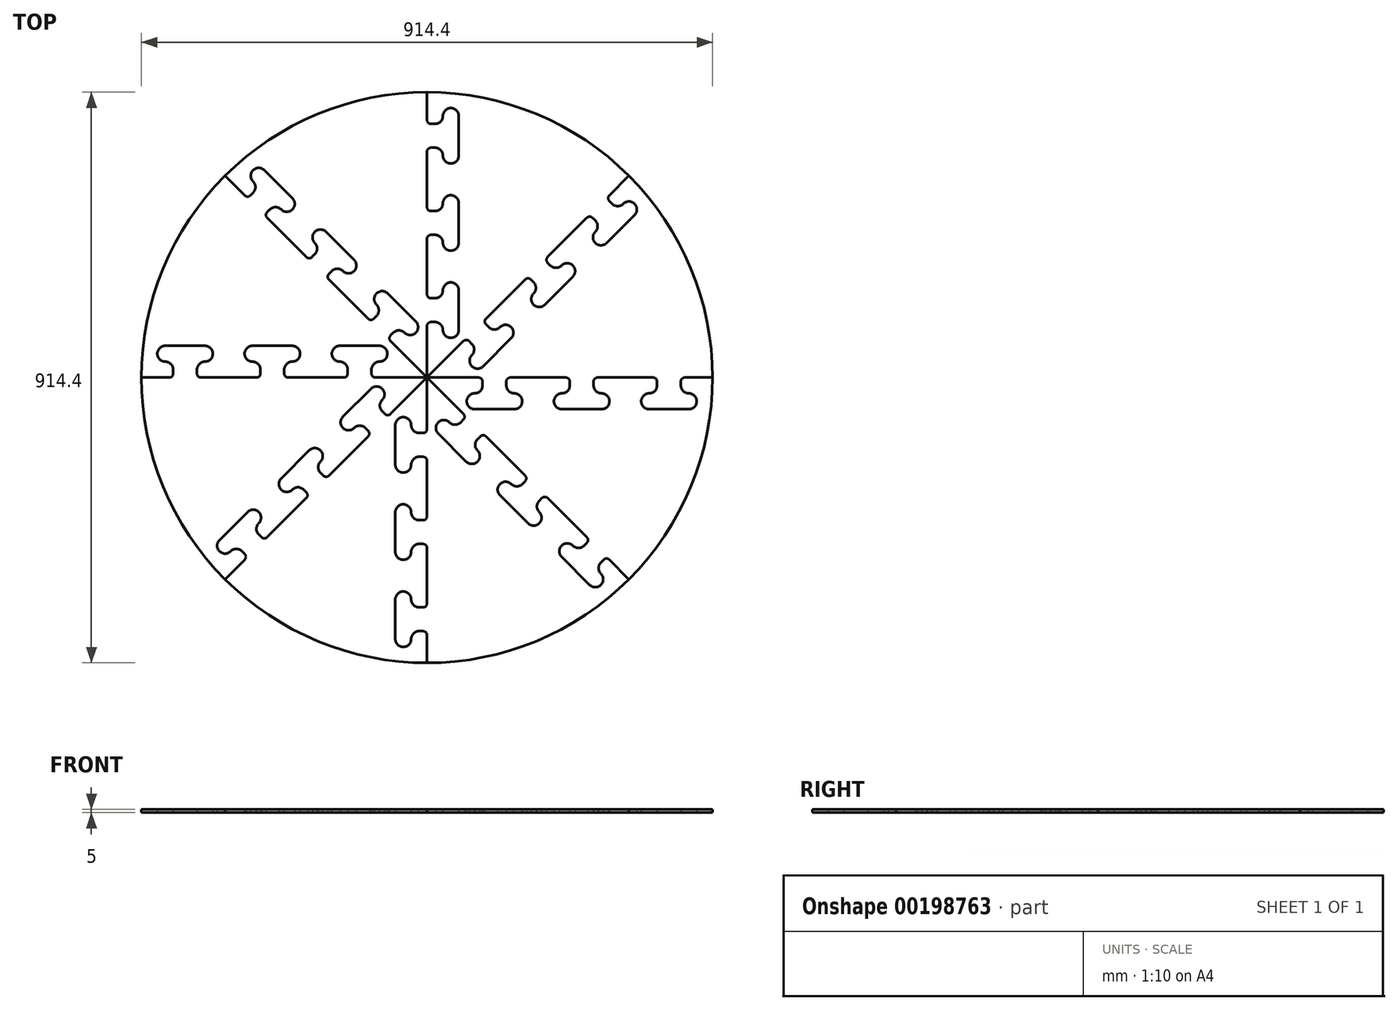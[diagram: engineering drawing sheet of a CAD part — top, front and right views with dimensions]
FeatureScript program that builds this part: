
annotation { "Feature Type Name" : "Feature", "Feature Type Description" : "" }
export const myFeature = defineFeature(function(context is Context, id is Id, definition is map)
    precondition{}
    {
        {
            var Q0;
            Q0=qCreatedBy(makeId("Top.planeOp"),FACE);
            var sketch = newSketch(context, id + "F0", { "sketchPlane" : qUnion([Q0])});
            skLineSegment(sketch, "E0", {"start": v(-457.2, 0) * mm, "end": v(-412.75, 0) * mm});
            skLineSegment(sketch, "E1", {"start": v(-406.4, 6.35) * mm, "end": v(-406.4, 12.7) * mm});
            skArc(sketch, "E2", {"start": v(-419.1, 50.8) * mm, "mid": v(-431.8, 38.1) * mm, "end": v(-419.1, 25.4) * mm});
            skLineSegment(sketch, "E3", {"start": v(-387.35, 0) * mm, "end": v(-387.35, 50.8) * mm, "construction": true});
            skLineSegment(sketch, "E4", {"start": v(-419.1, 50.8) * mm, "end": v(-387.35, 50.8) * mm});
            skPoint(sketch, "E5.visualSharp", {"position": v(-406.4, 38.1) * mm});
            skArc(sketch, "E5.filletArc", {"start": v(-406.4, 12.7) * mm, "mid": v(-410.12, 21.68) * mm, "end": v(-419.1, 25.4) * mm});
            skLineSegment(sketch, "E6", {"start": v(-406.4, 0) * mm, "end": v(-387.35, 0) * mm, "construction": true});
            skPoint(sketch, "E7.visualSharp", {"position": v(-406.4, 0) * mm});
            skArc(sketch, "E7.filletArc", {"start": v(-412.75, 0) * mm, "mid": v(-408.26, 1.86) * mm, "end": v(-406.4, 6.35) * mm});
            skLineSegment(sketch, "E8", {"start": v(-406.4, 0) * mm, "end": v(-406.4, 6.35) * mm, "construction": true});
            skLineSegment(sketch, "E9", {"start": v(-412.75, 0) * mm, "end": v(-406.4, 0) * mm, "construction": true});
            skLineSegment(sketch, "E10.MirrorCS", {"start": v(-355.6, 50.8) * mm, "end": v(-387.35, 50.8) * mm});
            skArc(sketch, "E11.MirrorCS", {"start": v(-355.6, 50.8) * mm, "mid": v(-342.9, 38.1) * mm, "end": v(-355.6, 25.4) * mm});
            skArc(sketch, "E12.MirrorCS", {"start": v(-368.3, 12.7) * mm, "mid": v(-364.58, 21.68) * mm, "end": v(-355.6, 25.4) * mm});
            skLineSegment(sketch, "E13.MirrorCS", {"start": v(-368.3, 6.35) * mm, "end": v(-368.3, 12.7) * mm});
            skArc(sketch, "E14.MirrorCS", {"start": v(-361.95, 0) * mm, "mid": v(-366.44, 1.86) * mm, "end": v(-368.3, 6.35) * mm});
            skLineSegment(sketch, "E15.1.0.0", {"start": v(-247.65, 0) * mm, "end": v(-247.65, 50.8) * mm, "construction": true});
            skPoint(sketch, "E15.1.0.1", {"position": v(-266.7, 38.1) * mm});
            skPoint(sketch, "E15.1.0.2", {"position": v(-266.7, 0) * mm});
            skArc(sketch, "E15.1.0.3", {"start": v(-279.4, 50.8) * mm, "mid": v(-292.1, 38.1) * mm, "end": v(-279.4, 25.4) * mm});
            skLineSegment(sketch, "E15.1.0.5", {"start": v(-266.7, 0) * mm, "end": v(-247.65, 0) * mm, "construction": true});
            skLineSegment(sketch, "E15.1.0.6", {"start": v(-215.9, 50.8) * mm, "end": v(-247.65, 50.8) * mm});
            skLineSegment(sketch, "E15.1.0.7", {"start": v(-279.4, 50.8) * mm, "end": v(-247.65, 50.8) * mm});
            skArc(sketch, "E15.1.0.8", {"start": v(-215.9, 50.8) * mm, "mid": v(-203.2, 38.1) * mm, "end": v(-215.9, 25.4) * mm});
            skLineSegment(sketch, "E15.1.0.9", {"start": v(-317.5, 0) * mm, "end": v(-273.05, 0) * mm});
            skArc(sketch, "E15.1.0.10", {"start": v(-266.7, 12.7) * mm, "mid": v(-270.42, 21.68) * mm, "end": v(-279.4, 25.4) * mm});
            skArc(sketch, "E15.1.0.11", {"start": v(-222.25, 0) * mm, "mid": v(-226.74, 1.86) * mm, "end": v(-228.6, 6.35) * mm});
            skArc(sketch, "E15.1.0.12", {"start": v(-228.6, 12.7) * mm, "mid": v(-224.88, 21.68) * mm, "end": v(-215.9, 25.4) * mm});
            skLineSegment(sketch, "E15.1.0.13", {"start": v(-228.6, 6.35) * mm, "end": v(-228.6, 12.7) * mm});
            skLineSegment(sketch, "E15.1.0.14", {"start": v(-266.7, 6.35) * mm, "end": v(-266.7, 12.7) * mm});
            skArc(sketch, "E15.1.0.15", {"start": v(-273.05, 0) * mm, "mid": v(-268.56, 1.86) * mm, "end": v(-266.7, 6.35) * mm});
            skLineSegment(sketch, "E15.1.0.16", {"start": v(-266.7, 0) * mm, "end": v(-266.7, 6.35) * mm, "construction": true});
            skLineSegment(sketch, "E15.1.0.17", {"start": v(-273.05, 0) * mm, "end": v(-266.7, 0) * mm, "construction": true});
            skLineSegment(sketch, "E15.2.0.0", {"start": v(-107.95, 0) * mm, "end": v(-107.95, 50.8) * mm, "construction": true});
            skPoint(sketch, "E15.2.0.1", {"position": v(-127, 38.1) * mm});
            skArc(sketch, "E15.2.0.3", {"start": v(-139.7, 50.8) * mm, "mid": v(-152.4, 38.1) * mm, "end": v(-139.7, 25.4) * mm});
            skLineSegment(sketch, "E15.2.0.5", {"start": v(-127, 0) * mm, "end": v(-107.95, 0) * mm, "construction": true});
            skLineSegment(sketch, "E15.2.0.6", {"start": v(-76.2, 50.8) * mm, "end": v(-107.95, 50.8) * mm});
            skLineSegment(sketch, "E15.2.0.7", {"start": v(-139.7, 50.8) * mm, "end": v(-107.95, 50.8) * mm});
            skArc(sketch, "E15.2.0.8", {"start": v(-76.2, 50.8) * mm, "mid": v(-63.5, 38.1) * mm, "end": v(-76.2, 25.4) * mm});
            skLineSegment(sketch, "E15.2.0.9", {"start": v(-177.8, 0) * mm, "end": v(-133.35, 0) * mm});
            skArc(sketch, "E15.2.0.10", {"start": v(-127, 12.7) * mm, "mid": v(-130.72, 21.68) * mm, "end": v(-139.7, 25.4) * mm});
            skArc(sketch, "E15.2.0.11", {"start": v(-82.55, 0) * mm, "mid": v(-87.04, 1.86) * mm, "end": v(-88.9, 6.35) * mm});
            skArc(sketch, "E15.2.0.12", {"start": v(-88.9, 12.7) * mm, "mid": v(-85.18, 21.68) * mm, "end": v(-76.2, 25.4) * mm});
            skLineSegment(sketch, "E15.2.0.13", {"start": v(-88.9, 6.35) * mm, "end": v(-88.9, 12.7) * mm});
            skLineSegment(sketch, "E15.2.0.14", {"start": v(-127, 6.35) * mm, "end": v(-127, 12.7) * mm});
            skArc(sketch, "E15.2.0.15", {"start": v(-133.35, 0) * mm, "mid": v(-128.86, 1.86) * mm, "end": v(-127, 6.35) * mm});
            skLineSegment(sketch, "E15.2.0.16", {"start": v(-127, 0) * mm, "end": v(-127, 6.35) * mm, "construction": true});
            skLineSegment(sketch, "E15.2.0.17", {"start": v(-133.35, 0) * mm, "end": v(-127, 0) * mm, "construction": true});
            skLineSegment(sketch, "E15.direction1", {"start": v(-457.2, 0) * mm, "end": v(-317.5, 0) * mm, "construction": true});
            skLineSegment(sketch, "E16", {"start": v(-361.95, 0) * mm, "end": v(-317.5, 0) * mm});
            skLineSegment(sketch, "E17", {"start": v(-222.25, 0) * mm, "end": v(-177.8, 0) * mm});
            skLineSegment(sketch, "E18", {"start": v(-82.55, 0) * mm, "end": v(0, 0) * mm});
            skCircle(sketch, "E19.1.0", {"center": v(0, 0) * mm, "radius": 457.2 * mm});
            skLineSegment(sketch, "E20", {"start": v(-419.1, 25.4) * mm, "end": v(-355.6, 25.4) * mm, "construction": true});
            skLineSegment(sketch, "E21.1.0", {"start": v(-224.5, -224.5) * mm, "end": v(-193.08, -193.08) * mm});
            skLineSegment(sketch, "E21.1.1", {"start": v(-89.8, -89.8) * mm, "end": v(-76.33, -76.33) * mm, "construction": true});
            skArc(sketch, "E21.1.2", {"start": v(-296.35, -278.39) * mm, "mid": v(-305.33, -274.67) * mm, "end": v(-314.3, -278.39) * mm});
            skLineSegment(sketch, "E21.1.3", {"start": v(-323.29, -323.29) * mm, "end": v(-224.5, -224.5) * mm, "construction": true});
            skLineSegment(sketch, "E21.1.4", {"start": v(-175.11, -175.11) * mm, "end": v(-211.04, -139.2) * mm, "construction": true});
            skPoint(sketch, "E21.1.5", {"position": v(-188.59, -188.59) * mm});
            skArc(sketch, "E21.1.6", {"start": v(-269.4, -251.45) * mm, "mid": v(-273.13, -242.47) * mm, "end": v(-269.4, -233.49) * mm});
            skLineSegment(sketch, "E21.1.7", {"start": v(-287.37, -215.53) * mm, "end": v(-309.82, -237.98) * mm});
            skLineSegment(sketch, "E21.1.8", {"start": v(-332.27, -260.43) * mm, "end": v(-309.82, -237.98) * mm});
            skPoint(sketch, "E21.1.9", {"position": v(-314.3, -260.43) * mm});
            skArc(sketch, "E21.1.10", {"start": v(-332.27, -260.43) * mm, "mid": v(-332.27, -278.39) * mm, "end": v(-314.3, -278.39) * mm});
            skLineSegment(sketch, "E21.1.11", {"start": v(-273.9, -273.9) * mm, "end": v(-309.82, -237.98) * mm, "construction": true});
            skLineSegment(sketch, "E21.1.12", {"start": v(-157.15, -157.15) * mm, "end": v(-125.72, -125.72) * mm});
            skArc(sketch, "E21.1.13", {"start": v(-197.57, -179.6) * mm, "mid": v(-206.55, -175.89) * mm, "end": v(-215.53, -179.6) * mm});
            skArc(sketch, "E21.1.14", {"start": v(-89.8, -17.96) * mm, "mid": v(-71.84, -17.96) * mm, "end": v(-71.84, -35.92) * mm});
            skArc(sketch, "E21.1.15", {"start": v(-233.49, -161.64) * mm, "mid": v(-233.49, -179.6) * mm, "end": v(-215.53, -179.6) * mm});
            skLineSegment(sketch, "E21.1.16", {"start": v(-188.59, -188.59) * mm, "end": v(-175.11, -175.11) * mm, "construction": true});
            skArc(sketch, "E21.1.17", {"start": v(-98.78, -80.82) * mm, "mid": v(-107.76, -77.1) * mm, "end": v(-116.74, -80.82) * mm});
            skLineSegment(sketch, "E21.1.18", {"start": v(-233.49, -161.64) * mm, "end": v(-211.04, -139.2) * mm});
            skLineSegment(sketch, "E21.1.19", {"start": v(-134.7, -62.86) * mm, "end": v(-112.25, -40.41) * mm});
            skLineSegment(sketch, "E21.1.20", {"start": v(-188.59, -116.74) * mm, "end": v(-211.04, -139.2) * mm});
            skLineSegment(sketch, "E21.1.21", {"start": v(-314.3, -278.39) * mm, "end": v(-269.4, -233.49) * mm, "construction": true});
            skLineSegment(sketch, "E21.1.22", {"start": v(-76.33, -76.33) * mm, "end": v(-112.25, -40.41) * mm, "construction": true});
            skPoint(sketch, "E21.1.23", {"position": v(-116.74, -62.86) * mm});
            skLineSegment(sketch, "E21.1.24", {"start": v(-125.72, -125.72) * mm, "end": v(-94.3, -94.3) * mm});
            skLineSegment(sketch, "E21.1.25", {"start": v(-58.37, -58.37) * mm, "end": v(0, 0) * mm});
            skLineSegment(sketch, "E21.1.26", {"start": v(-89.8, -17.96) * mm, "end": v(-112.25, -40.41) * mm});
            skArc(sketch, "E21.1.27", {"start": v(-188.59, -116.74) * mm, "mid": v(-170.62, -116.74) * mm, "end": v(-170.62, -134.7) * mm});
            skArc(sketch, "E21.1.28", {"start": v(-71.84, -53.88) * mm, "mid": v(-75.56, -44.9) * mm, "end": v(-71.84, -35.92) * mm});
            skPoint(sketch, "E21.1.29", {"position": v(-287.37, -287.37) * mm});
            skArc(sketch, "E21.1.30", {"start": v(-170.62, -152.66) * mm, "mid": v(-174.34, -143.68) * mm, "end": v(-170.62, -134.7) * mm});
            skArc(sketch, "E21.1.31", {"start": v(-134.7, -62.86) * mm, "mid": v(-134.7, -80.82) * mm, "end": v(-116.74, -80.82) * mm});
            skPoint(sketch, "E21.1.32", {"position": v(-215.53, -161.64) * mm});
            skArc(sketch, "E21.1.33", {"start": v(-287.37, -215.53) * mm, "mid": v(-269.4, -215.53) * mm, "end": v(-269.4, -233.49) * mm});
            skLineSegment(sketch, "E21.1.34", {"start": v(-255.94, -255.94) * mm, "end": v(-224.5, -224.5) * mm});
            skLineSegment(sketch, "E21.1.35", {"start": v(-323.29, -323.29) * mm, "end": v(-291.86, -291.86) * mm});
            skLineSegment(sketch, "E21.1.36", {"start": v(-287.37, -287.37) * mm, "end": v(-273.9, -273.9) * mm, "construction": true});
            skLineSegment(sketch, "E21.1.37", {"start": v(-193.08, -184.1) * mm, "end": v(-197.57, -179.6) * mm});
            skLineSegment(sketch, "E21.1.38", {"start": v(-264.92, -255.94) * mm, "end": v(-269.4, -251.45) * mm});
            skLineSegment(sketch, "E21.1.39", {"start": v(-166.13, -157.15) * mm, "end": v(-170.62, -152.66) * mm});
            skArc(sketch, "E21.1.40", {"start": v(-255.94, -255.94) * mm, "mid": v(-260.43, -257.8) * mm, "end": v(-264.92, -255.94) * mm});
            skLineSegment(sketch, "E21.1.41", {"start": v(-94.3, -85.31) * mm, "end": v(-98.78, -80.82) * mm});
            skArc(sketch, "E21.1.42", {"start": v(-157.15, -157.15) * mm, "mid": v(-161.64, -159.01) * mm, "end": v(-166.13, -157.15) * mm});
            skLineSegment(sketch, "E21.1.43", {"start": v(-291.86, -282.88) * mm, "end": v(-296.35, -278.39) * mm});
            skArc(sketch, "E21.1.44", {"start": v(-58.37, -58.37) * mm, "mid": v(-62.86, -60.23) * mm, "end": v(-67.35, -58.37) * mm});
            skLineSegment(sketch, "E21.1.45", {"start": v(-67.35, -58.37) * mm, "end": v(-71.84, -53.88) * mm});
            skArc(sketch, "E21.1.46", {"start": v(-94.3, -94.3) * mm, "mid": v(-92.43, -89.8) * mm, "end": v(-94.3, -85.31) * mm});
            skLineSegment(sketch, "E21.1.47", {"start": v(-291.86, -291.86) * mm, "end": v(-287.37, -287.37) * mm, "construction": true});
            skLineSegment(sketch, "E21.1.48", {"start": v(-94.3, -94.3) * mm, "end": v(-89.8, -89.8) * mm, "construction": true});
            skLineSegment(sketch, "E21.1.49", {"start": v(-193.08, -193.08) * mm, "end": v(-188.59, -188.59) * mm, "construction": true});
            skLineSegment(sketch, "E21.1.50", {"start": v(-188.59, -188.59) * mm, "end": v(-193.08, -184.1) * mm, "construction": true});
            skLineSegment(sketch, "E21.1.51", {"start": v(-89.8, -89.8) * mm, "end": v(-94.3, -85.31) * mm, "construction": true});
            skLineSegment(sketch, "E21.1.52", {"start": v(-287.37, -287.37) * mm, "end": v(-291.86, -282.88) * mm, "construction": true});
            skArc(sketch, "E21.1.53", {"start": v(-193.08, -193.08) * mm, "mid": v(-191.22, -188.59) * mm, "end": v(-193.08, -184.1) * mm});
            skArc(sketch, "E21.1.54", {"start": v(-291.86, -291.86) * mm, "mid": v(-290, -287.37) * mm, "end": v(-291.86, -282.88) * mm});
            skLineSegment(sketch, "E21.2.0", {"start": v(0, -317.5) * mm, "end": v(0, -273.05) * mm});
            skLineSegment(sketch, "E21.2.1", {"start": v(0, -127) * mm, "end": v(0, -107.95) * mm, "construction": true});
            skArc(sketch, "E21.2.2", {"start": v(-12.7, -406.4) * mm, "mid": v(-21.68, -410.12) * mm, "end": v(-25.4, -419.1) * mm});
            skLineSegment(sketch, "E21.2.3", {"start": v(0, -457.2) * mm, "end": v(0, -317.5) * mm, "construction": true});
            skLineSegment(sketch, "E21.2.4", {"start": v(0, -247.65) * mm, "end": v(-50.8, -247.65) * mm, "construction": true});
            skPoint(sketch, "E21.2.5", {"position": v(0, -266.7) * mm});
            skArc(sketch, "E21.2.6", {"start": v(-12.7, -368.3) * mm, "mid": v(-21.68, -364.58) * mm, "end": v(-25.4, -355.6) * mm});
            skLineSegment(sketch, "E21.2.7", {"start": v(-50.8, -355.6) * mm, "end": v(-50.8, -387.35) * mm});
            skLineSegment(sketch, "E21.2.8", {"start": v(-50.8, -419.1) * mm, "end": v(-50.8, -387.35) * mm});
            skPoint(sketch, "E21.2.9", {"position": v(-38.1, -406.4) * mm});
            skArc(sketch, "E21.2.10", {"start": v(-50.8, -419.1) * mm, "mid": v(-38.1, -431.8) * mm, "end": v(-25.4, -419.1) * mm});
            skLineSegment(sketch, "E21.2.11", {"start": v(0, -387.35) * mm, "end": v(-50.8, -387.35) * mm, "construction": true});
            skLineSegment(sketch, "E21.2.12", {"start": v(0, -222.25) * mm, "end": v(0, -177.8) * mm});
            skArc(sketch, "E21.2.13", {"start": v(-12.7, -266.7) * mm, "mid": v(-21.68, -270.42) * mm, "end": v(-25.4, -279.4) * mm});
            skArc(sketch, "E21.2.14", {"start": v(-50.8, -76.2) * mm, "mid": v(-38.1, -63.5) * mm, "end": v(-25.4, -76.2) * mm});
            skArc(sketch, "E21.2.15", {"start": v(-50.8, -279.4) * mm, "mid": v(-38.1, -292.1) * mm, "end": v(-25.4, -279.4) * mm});
            skLineSegment(sketch, "E21.2.16", {"start": v(0, -266.7) * mm, "end": v(0, -247.65) * mm, "construction": true});
            skArc(sketch, "E21.2.17", {"start": v(-12.7, -127) * mm, "mid": v(-21.68, -130.72) * mm, "end": v(-25.4, -139.7) * mm});
            skLineSegment(sketch, "E21.2.18", {"start": v(-50.8, -279.4) * mm, "end": v(-50.8, -247.65) * mm});
            skLineSegment(sketch, "E21.2.19", {"start": v(-50.8, -139.7) * mm, "end": v(-50.8, -107.95) * mm});
            skLineSegment(sketch, "E21.2.20", {"start": v(-50.8, -215.9) * mm, "end": v(-50.8, -247.65) * mm});
            skLineSegment(sketch, "E21.2.21", {"start": v(-25.4, -419.1) * mm, "end": v(-25.4, -355.6) * mm, "construction": true});
            skLineSegment(sketch, "E21.2.22", {"start": v(0, -107.95) * mm, "end": v(-50.8, -107.95) * mm, "construction": true});
            skPoint(sketch, "E21.2.23", {"position": v(-38.1, -127) * mm});
            skLineSegment(sketch, "E21.2.24", {"start": v(0, -177.8) * mm, "end": v(0, -133.35) * mm});
            skLineSegment(sketch, "E21.2.25", {"start": v(0, -82.55) * mm, "end": v(0, 0) * mm});
            skLineSegment(sketch, "E21.2.26", {"start": v(-50.8, -76.2) * mm, "end": v(-50.8, -107.95) * mm});
            skArc(sketch, "E21.2.27", {"start": v(-50.8, -215.9) * mm, "mid": v(-38.1, -203.2) * mm, "end": v(-25.4, -215.9) * mm});
            skArc(sketch, "E21.2.28", {"start": v(-12.7, -88.9) * mm, "mid": v(-21.68, -85.18) * mm, "end": v(-25.4, -76.2) * mm});
            skPoint(sketch, "E21.2.29", {"position": v(0, -406.4) * mm});
            skArc(sketch, "E21.2.30", {"start": v(-12.7, -228.6) * mm, "mid": v(-21.68, -224.88) * mm, "end": v(-25.4, -215.9) * mm});
            skArc(sketch, "E21.2.31", {"start": v(-50.8, -139.7) * mm, "mid": v(-38.1, -152.4) * mm, "end": v(-25.4, -139.7) * mm});
            skPoint(sketch, "E21.2.32", {"position": v(-38.1, -266.7) * mm});
            skArc(sketch, "E21.2.33", {"start": v(-50.8, -355.6) * mm, "mid": v(-38.1, -342.9) * mm, "end": v(-25.4, -355.6) * mm});
            skLineSegment(sketch, "E21.2.34", {"start": v(0, -361.95) * mm, "end": v(0, -317.5) * mm});
            skLineSegment(sketch, "E21.2.35", {"start": v(0, -457.2) * mm, "end": v(0, -412.75) * mm});
            skLineSegment(sketch, "E21.2.36", {"start": v(0, -406.4) * mm, "end": v(0, -387.35) * mm, "construction": true});
            skLineSegment(sketch, "E21.2.37", {"start": v(-6.35, -266.7) * mm, "end": v(-12.7, -266.7) * mm});
            skLineSegment(sketch, "E21.2.38", {"start": v(-6.35, -368.3) * mm, "end": v(-12.7, -368.3) * mm});
            skLineSegment(sketch, "E21.2.39", {"start": v(-6.35, -228.6) * mm, "end": v(-12.7, -228.6) * mm});
            skArc(sketch, "E21.2.40", {"start": v(0, -361.95) * mm, "mid": v(-1.86, -366.44) * mm, "end": v(-6.35, -368.3) * mm});
            skLineSegment(sketch, "E21.2.41", {"start": v(-6.35, -127) * mm, "end": v(-12.7, -127) * mm});
            skArc(sketch, "E21.2.42", {"start": v(0, -222.25) * mm, "mid": v(-1.86, -226.74) * mm, "end": v(-6.35, -228.6) * mm});
            skLineSegment(sketch, "E21.2.43", {"start": v(-6.35, -406.4) * mm, "end": v(-12.7, -406.4) * mm});
            skArc(sketch, "E21.2.44", {"start": v(0, -82.55) * mm, "mid": v(-1.86, -87.04) * mm, "end": v(-6.35, -88.9) * mm});
            skLineSegment(sketch, "E21.2.45", {"start": v(-6.35, -88.9) * mm, "end": v(-12.7, -88.9) * mm});
            skArc(sketch, "E21.2.46", {"start": v(0, -133.35) * mm, "mid": v(-1.86, -128.86) * mm, "end": v(-6.35, -127) * mm});
            skLineSegment(sketch, "E21.2.47", {"start": v(0, -412.75) * mm, "end": v(0, -406.4) * mm, "construction": true});
            skLineSegment(sketch, "E21.2.48", {"start": v(0, -133.35) * mm, "end": v(0, -127) * mm, "construction": true});
            skLineSegment(sketch, "E21.2.49", {"start": v(0, -273.05) * mm, "end": v(0, -266.7) * mm, "construction": true});
            skLineSegment(sketch, "E21.2.50", {"start": v(0, -266.7) * mm, "end": v(-6.35, -266.7) * mm, "construction": true});
            skLineSegment(sketch, "E21.2.51", {"start": v(0, -127) * mm, "end": v(-6.35, -127) * mm, "construction": true});
            skLineSegment(sketch, "E21.2.52", {"start": v(0, -406.4) * mm, "end": v(-6.35, -406.4) * mm, "construction": true});
            skArc(sketch, "E21.2.53", {"start": v(0, -273.05) * mm, "mid": v(-1.86, -268.56) * mm, "end": v(-6.35, -266.7) * mm});
            skArc(sketch, "E21.2.54", {"start": v(0, -412.75) * mm, "mid": v(-1.86, -408.26) * mm, "end": v(-6.35, -406.4) * mm});
            skLineSegment(sketch, "E21.3.0", {"start": v(224.5, -224.5) * mm, "end": v(193.08, -193.08) * mm});
            skLineSegment(sketch, "E21.3.1", {"start": v(89.8, -89.8) * mm, "end": v(76.33, -76.33) * mm, "construction": true});
            skArc(sketch, "E21.3.2", {"start": v(278.39, -296.35) * mm, "mid": v(274.67, -305.33) * mm, "end": v(278.39, -314.3) * mm});
            skLineSegment(sketch, "E21.3.3", {"start": v(323.29, -323.29) * mm, "end": v(224.5, -224.5) * mm, "construction": true});
            skLineSegment(sketch, "E21.3.4", {"start": v(175.11, -175.11) * mm, "end": v(139.2, -211.04) * mm, "construction": true});
            skPoint(sketch, "E21.3.5", {"position": v(188.59, -188.59) * mm});
            skArc(sketch, "E21.3.6", {"start": v(251.45, -269.4) * mm, "mid": v(242.47, -273.13) * mm, "end": v(233.49, -269.4) * mm});
            skLineSegment(sketch, "E21.3.7", {"start": v(215.53, -287.37) * mm, "end": v(237.98, -309.82) * mm});
            skLineSegment(sketch, "E21.3.8", {"start": v(260.43, -332.27) * mm, "end": v(237.98, -309.82) * mm});
            skPoint(sketch, "E21.3.9", {"position": v(260.43, -314.3) * mm});
            skArc(sketch, "E21.3.10", {"start": v(260.43, -332.27) * mm, "mid": v(278.39, -332.27) * mm, "end": v(278.39, -314.3) * mm});
            skLineSegment(sketch, "E21.3.11", {"start": v(273.9, -273.9) * mm, "end": v(237.98, -309.82) * mm, "construction": true});
            skLineSegment(sketch, "E21.3.12", {"start": v(157.15, -157.15) * mm, "end": v(125.72, -125.72) * mm});
            skArc(sketch, "E21.3.13", {"start": v(179.6, -197.57) * mm, "mid": v(175.89, -206.55) * mm, "end": v(179.6, -215.53) * mm});
            skArc(sketch, "E21.3.14", {"start": v(17.96, -89.8) * mm, "mid": v(17.96, -71.84) * mm, "end": v(35.92, -71.84) * mm});
            skArc(sketch, "E21.3.15", {"start": v(161.64, -233.49) * mm, "mid": v(179.6, -233.49) * mm, "end": v(179.6, -215.53) * mm});
            skLineSegment(sketch, "E21.3.16", {"start": v(188.59, -188.59) * mm, "end": v(175.11, -175.11) * mm, "construction": true});
            skArc(sketch, "E21.3.17", {"start": v(80.82, -98.78) * mm, "mid": v(77.1, -107.76) * mm, "end": v(80.82, -116.74) * mm});
            skLineSegment(sketch, "E21.3.18", {"start": v(161.64, -233.49) * mm, "end": v(139.2, -211.04) * mm});
            skLineSegment(sketch, "E21.3.19", {"start": v(62.86, -134.7) * mm, "end": v(40.41, -112.25) * mm});
            skLineSegment(sketch, "E21.3.20", {"start": v(116.74, -188.59) * mm, "end": v(139.2, -211.04) * mm});
            skLineSegment(sketch, "E21.3.21", {"start": v(278.39, -314.3) * mm, "end": v(233.49, -269.4) * mm, "construction": true});
            skLineSegment(sketch, "E21.3.22", {"start": v(76.33, -76.33) * mm, "end": v(40.41, -112.25) * mm, "construction": true});
            skPoint(sketch, "E21.3.23", {"position": v(62.86, -116.74) * mm});
            skLineSegment(sketch, "E21.3.24", {"start": v(125.72, -125.72) * mm, "end": v(94.3, -94.3) * mm});
            skLineSegment(sketch, "E21.3.25", {"start": v(58.37, -58.37) * mm, "end": v(0, 0) * mm});
            skLineSegment(sketch, "E21.3.26", {"start": v(17.96, -89.8) * mm, "end": v(40.41, -112.25) * mm});
            skArc(sketch, "E21.3.27", {"start": v(116.74, -188.59) * mm, "mid": v(116.74, -170.62) * mm, "end": v(134.7, -170.62) * mm});
            skArc(sketch, "E21.3.28", {"start": v(53.88, -71.84) * mm, "mid": v(44.9, -75.56) * mm, "end": v(35.92, -71.84) * mm});
            skPoint(sketch, "E21.3.29", {"position": v(287.37, -287.37) * mm});
            skArc(sketch, "E21.3.30", {"start": v(152.66, -170.62) * mm, "mid": v(143.68, -174.34) * mm, "end": v(134.7, -170.62) * mm});
            skArc(sketch, "E21.3.31", {"start": v(62.86, -134.7) * mm, "mid": v(80.82, -134.7) * mm, "end": v(80.82, -116.74) * mm});
            skPoint(sketch, "E21.3.32", {"position": v(161.64, -215.53) * mm});
            skArc(sketch, "E21.3.33", {"start": v(215.53, -287.37) * mm, "mid": v(215.53, -269.4) * mm, "end": v(233.49, -269.4) * mm});
            skLineSegment(sketch, "E21.3.34", {"start": v(255.94, -255.94) * mm, "end": v(224.5, -224.5) * mm});
            skLineSegment(sketch, "E21.3.35", {"start": v(323.29, -323.29) * mm, "end": v(291.86, -291.86) * mm});
            skLineSegment(sketch, "E21.3.36", {"start": v(287.37, -287.37) * mm, "end": v(273.9, -273.9) * mm, "construction": true});
            skLineSegment(sketch, "E21.3.37", {"start": v(184.1, -193.08) * mm, "end": v(179.6, -197.57) * mm});
            skLineSegment(sketch, "E21.3.38", {"start": v(255.94, -264.92) * mm, "end": v(251.45, -269.4) * mm});
            skLineSegment(sketch, "E21.3.39", {"start": v(157.15, -166.13) * mm, "end": v(152.66, -170.62) * mm});
            skArc(sketch, "E21.3.40", {"start": v(255.94, -255.94) * mm, "mid": v(257.8, -260.43) * mm, "end": v(255.94, -264.92) * mm});
            skLineSegment(sketch, "E21.3.41", {"start": v(85.31, -94.3) * mm, "end": v(80.82, -98.78) * mm});
            skArc(sketch, "E21.3.42", {"start": v(157.15, -157.15) * mm, "mid": v(159.01, -161.64) * mm, "end": v(157.15, -166.13) * mm});
            skLineSegment(sketch, "E21.3.43", {"start": v(282.88, -291.86) * mm, "end": v(278.39, -296.35) * mm});
            skArc(sketch, "E21.3.44", {"start": v(58.37, -58.37) * mm, "mid": v(60.23, -62.86) * mm, "end": v(58.37, -67.35) * mm});
            skLineSegment(sketch, "E21.3.45", {"start": v(58.37, -67.35) * mm, "end": v(53.88, -71.84) * mm});
            skArc(sketch, "E21.3.46", {"start": v(94.3, -94.3) * mm, "mid": v(89.8, -92.43) * mm, "end": v(85.31, -94.3) * mm});
            skLineSegment(sketch, "E21.3.47", {"start": v(291.86, -291.86) * mm, "end": v(287.37, -287.37) * mm, "construction": true});
            skLineSegment(sketch, "E21.3.48", {"start": v(94.3, -94.3) * mm, "end": v(89.8, -89.8) * mm, "construction": true});
            skLineSegment(sketch, "E21.3.49", {"start": v(193.08, -193.08) * mm, "end": v(188.59, -188.59) * mm, "construction": true});
            skLineSegment(sketch, "E21.3.50", {"start": v(188.59, -188.59) * mm, "end": v(184.1, -193.08) * mm, "construction": true});
            skLineSegment(sketch, "E21.3.51", {"start": v(89.8, -89.8) * mm, "end": v(85.31, -94.3) * mm, "construction": true});
            skLineSegment(sketch, "E21.3.52", {"start": v(287.37, -287.37) * mm, "end": v(282.88, -291.86) * mm, "construction": true});
            skArc(sketch, "E21.3.53", {"start": v(193.08, -193.08) * mm, "mid": v(188.59, -191.22) * mm, "end": v(184.1, -193.08) * mm});
            skArc(sketch, "E21.3.54", {"start": v(291.86, -291.86) * mm, "mid": v(287.37, -290) * mm, "end": v(282.88, -291.86) * mm});
            skLineSegment(sketch, "E21.4.0", {"start": v(317.5, 0) * mm, "end": v(273.05, 0) * mm});
            skLineSegment(sketch, "E21.4.1", {"start": v(127, 0) * mm, "end": v(107.95, 0) * mm, "construction": true});
            skArc(sketch, "E21.4.2", {"start": v(406.4, -12.7) * mm, "mid": v(410.12, -21.68) * mm, "end": v(419.1, -25.4) * mm});
            skLineSegment(sketch, "E21.4.3", {"start": v(457.2, 0) * mm, "end": v(317.5, 0) * mm, "construction": true});
            skLineSegment(sketch, "E21.4.4", {"start": v(247.65, 0) * mm, "end": v(247.65, -50.8) * mm, "construction": true});
            skPoint(sketch, "E21.4.5", {"position": v(266.7, 0) * mm});
            skArc(sketch, "E21.4.6", {"start": v(368.3, -12.7) * mm, "mid": v(364.58, -21.68) * mm, "end": v(355.6, -25.4) * mm});
            skLineSegment(sketch, "E21.4.7", {"start": v(355.6, -50.8) * mm, "end": v(387.35, -50.8) * mm});
            skLineSegment(sketch, "E21.4.8", {"start": v(419.1, -50.8) * mm, "end": v(387.35, -50.8) * mm});
            skPoint(sketch, "E21.4.9", {"position": v(406.4, -38.1) * mm});
            skArc(sketch, "E21.4.10", {"start": v(419.1, -50.8) * mm, "mid": v(431.8, -38.1) * mm, "end": v(419.1, -25.4) * mm});
            skLineSegment(sketch, "E21.4.11", {"start": v(387.35, 0) * mm, "end": v(387.35, -50.8) * mm, "construction": true});
            skLineSegment(sketch, "E21.4.12", {"start": v(222.25, 0) * mm, "end": v(177.8, 0) * mm});
            skArc(sketch, "E21.4.13", {"start": v(266.7, -12.7) * mm, "mid": v(270.42, -21.68) * mm, "end": v(279.4, -25.4) * mm});
            skArc(sketch, "E21.4.14", {"start": v(76.2, -50.8) * mm, "mid": v(63.5, -38.1) * mm, "end": v(76.2, -25.4) * mm});
            skArc(sketch, "E21.4.15", {"start": v(279.4, -50.8) * mm, "mid": v(292.1, -38.1) * mm, "end": v(279.4, -25.4) * mm});
            skLineSegment(sketch, "E21.4.16", {"start": v(266.7, 0) * mm, "end": v(247.65, 0) * mm, "construction": true});
            skArc(sketch, "E21.4.17", {"start": v(127, -12.7) * mm, "mid": v(130.72, -21.68) * mm, "end": v(139.7, -25.4) * mm});
            skLineSegment(sketch, "E21.4.18", {"start": v(279.4, -50.8) * mm, "end": v(247.65, -50.8) * mm});
            skLineSegment(sketch, "E21.4.19", {"start": v(139.7, -50.8) * mm, "end": v(107.95, -50.8) * mm});
            skLineSegment(sketch, "E21.4.20", {"start": v(215.9, -50.8) * mm, "end": v(247.65, -50.8) * mm});
            skLineSegment(sketch, "E21.4.21", {"start": v(419.1, -25.4) * mm, "end": v(355.6, -25.4) * mm, "construction": true});
            skLineSegment(sketch, "E21.4.22", {"start": v(107.95, 0) * mm, "end": v(107.95, -50.8) * mm, "construction": true});
            skPoint(sketch, "E21.4.23", {"position": v(127, -38.1) * mm});
            skLineSegment(sketch, "E21.4.24", {"start": v(177.8, 0) * mm, "end": v(133.35, 0) * mm});
            skLineSegment(sketch, "E21.4.25", {"start": v(82.55, 0) * mm, "end": v(0, 0) * mm});
            skLineSegment(sketch, "E21.4.26", {"start": v(76.2, -50.8) * mm, "end": v(107.95, -50.8) * mm});
            skArc(sketch, "E21.4.27", {"start": v(215.9, -50.8) * mm, "mid": v(203.2, -38.1) * mm, "end": v(215.9, -25.4) * mm});
            skArc(sketch, "E21.4.28", {"start": v(88.9, -12.7) * mm, "mid": v(85.18, -21.68) * mm, "end": v(76.2, -25.4) * mm});
            skPoint(sketch, "E21.4.29", {"position": v(406.4, 0) * mm});
            skArc(sketch, "E21.4.30", {"start": v(228.6, -12.7) * mm, "mid": v(224.88, -21.68) * mm, "end": v(215.9, -25.4) * mm});
            skArc(sketch, "E21.4.31", {"start": v(139.7, -50.8) * mm, "mid": v(152.4, -38.1) * mm, "end": v(139.7, -25.4) * mm});
            skPoint(sketch, "E21.4.32", {"position": v(266.7, -38.1) * mm});
            skArc(sketch, "E21.4.33", {"start": v(355.6, -50.8) * mm, "mid": v(342.9, -38.1) * mm, "end": v(355.6, -25.4) * mm});
            skLineSegment(sketch, "E21.4.34", {"start": v(361.95, 0) * mm, "end": v(317.5, 0) * mm});
            skLineSegment(sketch, "E21.4.35", {"start": v(457.2, 0) * mm, "end": v(412.75, 0) * mm});
            skLineSegment(sketch, "E21.4.36", {"start": v(406.4, 0) * mm, "end": v(387.35, 0) * mm, "construction": true});
            skLineSegment(sketch, "E21.4.37", {"start": v(266.7, -6.35) * mm, "end": v(266.7, -12.7) * mm});
            skLineSegment(sketch, "E21.4.38", {"start": v(368.3, -6.35) * mm, "end": v(368.3, -12.7) * mm});
            skLineSegment(sketch, "E21.4.39", {"start": v(228.6, -6.35) * mm, "end": v(228.6, -12.7) * mm});
            skArc(sketch, "E21.4.40", {"start": v(361.95, 0) * mm, "mid": v(366.44, -1.86) * mm, "end": v(368.3, -6.35) * mm});
            skLineSegment(sketch, "E21.4.41", {"start": v(127, -6.35) * mm, "end": v(127, -12.7) * mm});
            skArc(sketch, "E21.4.42", {"start": v(222.25, 0) * mm, "mid": v(226.74, -1.86) * mm, "end": v(228.6, -6.35) * mm});
            skLineSegment(sketch, "E21.4.43", {"start": v(406.4, -6.35) * mm, "end": v(406.4, -12.7) * mm});
            skArc(sketch, "E21.4.44", {"start": v(82.55, 0) * mm, "mid": v(87.04, -1.86) * mm, "end": v(88.9, -6.35) * mm});
            skLineSegment(sketch, "E21.4.45", {"start": v(88.9, -6.35) * mm, "end": v(88.9, -12.7) * mm});
            skArc(sketch, "E21.4.46", {"start": v(133.35, 0) * mm, "mid": v(128.86, -1.86) * mm, "end": v(127, -6.35) * mm});
            skLineSegment(sketch, "E21.4.47", {"start": v(412.75, 0) * mm, "end": v(406.4, 0) * mm, "construction": true});
            skLineSegment(sketch, "E21.4.48", {"start": v(133.35, 0) * mm, "end": v(127, 0) * mm, "construction": true});
            skLineSegment(sketch, "E21.4.49", {"start": v(273.05, 0) * mm, "end": v(266.7, 0) * mm, "construction": true});
            skLineSegment(sketch, "E21.4.50", {"start": v(266.7, 0) * mm, "end": v(266.7, -6.35) * mm, "construction": true});
            skLineSegment(sketch, "E21.4.51", {"start": v(127, 0) * mm, "end": v(127, -6.35) * mm, "construction": true});
            skLineSegment(sketch, "E21.4.52", {"start": v(406.4, 0) * mm, "end": v(406.4, -6.35) * mm, "construction": true});
            skArc(sketch, "E21.4.53", {"start": v(273.05, 0) * mm, "mid": v(268.56, -1.86) * mm, "end": v(266.7, -6.35) * mm});
            skArc(sketch, "E21.4.54", {"start": v(412.75, 0) * mm, "mid": v(408.26, -1.86) * mm, "end": v(406.4, -6.35) * mm});
            skLineSegment(sketch, "E21.5.0", {"start": v(224.5, 224.5) * mm, "end": v(193.08, 193.08) * mm});
            skLineSegment(sketch, "E21.5.1", {"start": v(89.8, 89.8) * mm, "end": v(76.33, 76.33) * mm, "construction": true});
            skArc(sketch, "E21.5.2", {"start": v(296.35, 278.39) * mm, "mid": v(305.33, 274.67) * mm, "end": v(314.3, 278.39) * mm});
            skLineSegment(sketch, "E21.5.3", {"start": v(323.29, 323.29) * mm, "end": v(224.5, 224.5) * mm, "construction": true});
            skLineSegment(sketch, "E21.5.4", {"start": v(175.11, 175.11) * mm, "end": v(211.04, 139.2) * mm, "construction": true});
            skPoint(sketch, "E21.5.5", {"position": v(188.59, 188.59) * mm});
            skArc(sketch, "E21.5.6", {"start": v(269.4, 251.45) * mm, "mid": v(273.13, 242.47) * mm, "end": v(269.4, 233.49) * mm});
            skLineSegment(sketch, "E21.5.7", {"start": v(287.37, 215.53) * mm, "end": v(309.82, 237.98) * mm});
            skLineSegment(sketch, "E21.5.8", {"start": v(332.27, 260.43) * mm, "end": v(309.82, 237.98) * mm});
            skPoint(sketch, "E21.5.9", {"position": v(314.3, 260.43) * mm});
            skArc(sketch, "E21.5.10", {"start": v(332.27, 260.43) * mm, "mid": v(332.27, 278.39) * mm, "end": v(314.3, 278.39) * mm});
            skLineSegment(sketch, "E21.5.11", {"start": v(273.9, 273.9) * mm, "end": v(309.82, 237.98) * mm, "construction": true});
            skLineSegment(sketch, "E21.5.12", {"start": v(157.15, 157.15) * mm, "end": v(125.72, 125.72) * mm});
            skArc(sketch, "E21.5.13", {"start": v(197.57, 179.6) * mm, "mid": v(206.55, 175.89) * mm, "end": v(215.53, 179.6) * mm});
            skArc(sketch, "E21.5.14", {"start": v(89.8, 17.96) * mm, "mid": v(71.84, 17.96) * mm, "end": v(71.84, 35.92) * mm});
            skArc(sketch, "E21.5.15", {"start": v(233.49, 161.64) * mm, "mid": v(233.49, 179.6) * mm, "end": v(215.53, 179.6) * mm});
            skLineSegment(sketch, "E21.5.16", {"start": v(188.59, 188.59) * mm, "end": v(175.11, 175.11) * mm, "construction": true});
            skArc(sketch, "E21.5.17", {"start": v(98.78, 80.82) * mm, "mid": v(107.76, 77.1) * mm, "end": v(116.74, 80.82) * mm});
            skLineSegment(sketch, "E21.5.18", {"start": v(233.49, 161.64) * mm, "end": v(211.04, 139.2) * mm});
            skLineSegment(sketch, "E21.5.19", {"start": v(134.7, 62.86) * mm, "end": v(112.25, 40.41) * mm});
            skLineSegment(sketch, "E21.5.20", {"start": v(188.59, 116.74) * mm, "end": v(211.04, 139.2) * mm});
            skLineSegment(sketch, "E21.5.21", {"start": v(314.3, 278.39) * mm, "end": v(269.4, 233.49) * mm, "construction": true});
            skLineSegment(sketch, "E21.5.22", {"start": v(76.33, 76.33) * mm, "end": v(112.25, 40.41) * mm, "construction": true});
            skPoint(sketch, "E21.5.23", {"position": v(116.74, 62.86) * mm});
            skLineSegment(sketch, "E21.5.24", {"start": v(125.72, 125.72) * mm, "end": v(94.3, 94.3) * mm});
            skLineSegment(sketch, "E21.5.25", {"start": v(58.37, 58.37) * mm, "end": v(0, 0) * mm});
            skLineSegment(sketch, "E21.5.26", {"start": v(89.8, 17.96) * mm, "end": v(112.25, 40.41) * mm});
            skArc(sketch, "E21.5.27", {"start": v(188.59, 116.74) * mm, "mid": v(170.62, 116.74) * mm, "end": v(170.62, 134.7) * mm});
            skArc(sketch, "E21.5.28", {"start": v(71.84, 53.88) * mm, "mid": v(75.56, 44.9) * mm, "end": v(71.84, 35.92) * mm});
            skPoint(sketch, "E21.5.29", {"position": v(287.37, 287.37) * mm});
            skArc(sketch, "E21.5.30", {"start": v(170.62, 152.66) * mm, "mid": v(174.34, 143.68) * mm, "end": v(170.62, 134.7) * mm});
            skArc(sketch, "E21.5.31", {"start": v(134.7, 62.86) * mm, "mid": v(134.7, 80.82) * mm, "end": v(116.74, 80.82) * mm});
            skPoint(sketch, "E21.5.32", {"position": v(215.53, 161.64) * mm});
            skArc(sketch, "E21.5.33", {"start": v(287.37, 215.53) * mm, "mid": v(269.4, 215.53) * mm, "end": v(269.4, 233.49) * mm});
            skLineSegment(sketch, "E21.5.34", {"start": v(255.94, 255.94) * mm, "end": v(224.5, 224.5) * mm});
            skLineSegment(sketch, "E21.5.35", {"start": v(323.29, 323.29) * mm, "end": v(291.86, 291.86) * mm});
            skLineSegment(sketch, "E21.5.36", {"start": v(287.37, 287.37) * mm, "end": v(273.9, 273.9) * mm, "construction": true});
            skLineSegment(sketch, "E21.5.37", {"start": v(193.08, 184.1) * mm, "end": v(197.57, 179.6) * mm});
            skLineSegment(sketch, "E21.5.38", {"start": v(264.92, 255.94) * mm, "end": v(269.4, 251.45) * mm});
            skLineSegment(sketch, "E21.5.39", {"start": v(166.13, 157.15) * mm, "end": v(170.62, 152.66) * mm});
            skArc(sketch, "E21.5.40", {"start": v(255.94, 255.94) * mm, "mid": v(260.43, 257.8) * mm, "end": v(264.92, 255.94) * mm});
            skLineSegment(sketch, "E21.5.41", {"start": v(94.3, 85.31) * mm, "end": v(98.78, 80.82) * mm});
            skArc(sketch, "E21.5.42", {"start": v(157.15, 157.15) * mm, "mid": v(161.64, 159.01) * mm, "end": v(166.13, 157.15) * mm});
            skLineSegment(sketch, "E21.5.43", {"start": v(291.86, 282.88) * mm, "end": v(296.35, 278.39) * mm});
            skArc(sketch, "E21.5.44", {"start": v(58.37, 58.37) * mm, "mid": v(62.86, 60.23) * mm, "end": v(67.35, 58.37) * mm});
            skLineSegment(sketch, "E21.5.45", {"start": v(67.35, 58.37) * mm, "end": v(71.84, 53.88) * mm});
            skArc(sketch, "E21.5.46", {"start": v(94.3, 94.3) * mm, "mid": v(92.43, 89.8) * mm, "end": v(94.3, 85.31) * mm});
            skLineSegment(sketch, "E21.5.47", {"start": v(291.86, 291.86) * mm, "end": v(287.37, 287.37) * mm, "construction": true});
            skLineSegment(sketch, "E21.5.48", {"start": v(94.3, 94.3) * mm, "end": v(89.8, 89.8) * mm, "construction": true});
            skLineSegment(sketch, "E21.5.49", {"start": v(193.08, 193.08) * mm, "end": v(188.59, 188.59) * mm, "construction": true});
            skLineSegment(sketch, "E21.5.50", {"start": v(188.59, 188.59) * mm, "end": v(193.08, 184.1) * mm, "construction": true});
            skLineSegment(sketch, "E21.5.51", {"start": v(89.8, 89.8) * mm, "end": v(94.3, 85.31) * mm, "construction": true});
            skLineSegment(sketch, "E21.5.52", {"start": v(287.37, 287.37) * mm, "end": v(291.86, 282.88) * mm, "construction": true});
            skArc(sketch, "E21.5.53", {"start": v(193.08, 193.08) * mm, "mid": v(191.22, 188.59) * mm, "end": v(193.08, 184.1) * mm});
            skArc(sketch, "E21.5.54", {"start": v(291.86, 291.86) * mm, "mid": v(290, 287.37) * mm, "end": v(291.86, 282.88) * mm});
            skLineSegment(sketch, "E21.6.0", {"start": v(0, 317.5) * mm, "end": v(0, 273.05) * mm});
            skLineSegment(sketch, "E21.6.1", {"start": v(0, 127) * mm, "end": v(0, 107.95) * mm, "construction": true});
            skArc(sketch, "E21.6.2", {"start": v(12.7, 406.4) * mm, "mid": v(21.68, 410.12) * mm, "end": v(25.4, 419.1) * mm});
            skLineSegment(sketch, "E21.6.3", {"start": v(0, 457.2) * mm, "end": v(0, 317.5) * mm, "construction": true});
            skLineSegment(sketch, "E21.6.4", {"start": v(0, 247.65) * mm, "end": v(50.8, 247.65) * mm, "construction": true});
            skPoint(sketch, "E21.6.5", {"position": v(0, 266.7) * mm});
            skArc(sketch, "E21.6.6", {"start": v(12.7, 368.3) * mm, "mid": v(21.68, 364.58) * mm, "end": v(25.4, 355.6) * mm});
            skLineSegment(sketch, "E21.6.7", {"start": v(50.8, 355.6) * mm, "end": v(50.8, 387.35) * mm});
            skLineSegment(sketch, "E21.6.8", {"start": v(50.8, 419.1) * mm, "end": v(50.8, 387.35) * mm});
            skPoint(sketch, "E21.6.9", {"position": v(38.1, 406.4) * mm});
            skArc(sketch, "E21.6.10", {"start": v(50.8, 419.1) * mm, "mid": v(38.1, 431.8) * mm, "end": v(25.4, 419.1) * mm});
            skLineSegment(sketch, "E21.6.11", {"start": v(0, 387.35) * mm, "end": v(50.8, 387.35) * mm, "construction": true});
            skLineSegment(sketch, "E21.6.12", {"start": v(0, 222.25) * mm, "end": v(0, 177.8) * mm});
            skArc(sketch, "E21.6.13", {"start": v(12.7, 266.7) * mm, "mid": v(21.68, 270.42) * mm, "end": v(25.4, 279.4) * mm});
            skArc(sketch, "E21.6.14", {"start": v(50.8, 76.2) * mm, "mid": v(38.1, 63.5) * mm, "end": v(25.4, 76.2) * mm});
            skArc(sketch, "E21.6.15", {"start": v(50.8, 279.4) * mm, "mid": v(38.1, 292.1) * mm, "end": v(25.4, 279.4) * mm});
            skLineSegment(sketch, "E21.6.16", {"start": v(0, 266.7) * mm, "end": v(0, 247.65) * mm, "construction": true});
            skArc(sketch, "E21.6.17", {"start": v(12.7, 127) * mm, "mid": v(21.68, 130.72) * mm, "end": v(25.4, 139.7) * mm});
            skLineSegment(sketch, "E21.6.18", {"start": v(50.8, 279.4) * mm, "end": v(50.8, 247.65) * mm});
            skLineSegment(sketch, "E21.6.19", {"start": v(50.8, 139.7) * mm, "end": v(50.8, 107.95) * mm});
            skLineSegment(sketch, "E21.6.20", {"start": v(50.8, 215.9) * mm, "end": v(50.8, 247.65) * mm});
            skLineSegment(sketch, "E21.6.21", {"start": v(25.4, 419.1) * mm, "end": v(25.4, 355.6) * mm, "construction": true});
            skLineSegment(sketch, "E21.6.22", {"start": v(0, 107.95) * mm, "end": v(50.8, 107.95) * mm, "construction": true});
            skPoint(sketch, "E21.6.23", {"position": v(38.1, 127) * mm});
            skLineSegment(sketch, "E21.6.24", {"start": v(0, 177.8) * mm, "end": v(0, 133.35) * mm});
            skLineSegment(sketch, "E21.6.25", {"start": v(0, 82.55) * mm, "end": v(0, 0) * mm});
            skLineSegment(sketch, "E21.6.26", {"start": v(50.8, 76.2) * mm, "end": v(50.8, 107.95) * mm});
            skArc(sketch, "E21.6.27", {"start": v(50.8, 215.9) * mm, "mid": v(38.1, 203.2) * mm, "end": v(25.4, 215.9) * mm});
            skArc(sketch, "E21.6.28", {"start": v(12.7, 88.9) * mm, "mid": v(21.68, 85.18) * mm, "end": v(25.4, 76.2) * mm});
            skPoint(sketch, "E21.6.29", {"position": v(0, 406.4) * mm});
            skArc(sketch, "E21.6.30", {"start": v(12.7, 228.6) * mm, "mid": v(21.68, 224.88) * mm, "end": v(25.4, 215.9) * mm});
            skArc(sketch, "E21.6.31", {"start": v(50.8, 139.7) * mm, "mid": v(38.1, 152.4) * mm, "end": v(25.4, 139.7) * mm});
            skPoint(sketch, "E21.6.32", {"position": v(38.1, 266.7) * mm});
            skArc(sketch, "E21.6.33", {"start": v(50.8, 355.6) * mm, "mid": v(38.1, 342.9) * mm, "end": v(25.4, 355.6) * mm});
            skLineSegment(sketch, "E21.6.34", {"start": v(0, 361.95) * mm, "end": v(0, 317.5) * mm});
            skLineSegment(sketch, "E21.6.35", {"start": v(0, 457.2) * mm, "end": v(0, 412.75) * mm});
            skLineSegment(sketch, "E21.6.36", {"start": v(0, 406.4) * mm, "end": v(0, 387.35) * mm, "construction": true});
            skLineSegment(sketch, "E21.6.37", {"start": v(6.35, 266.7) * mm, "end": v(12.7, 266.7) * mm});
            skLineSegment(sketch, "E21.6.38", {"start": v(6.35, 368.3) * mm, "end": v(12.7, 368.3) * mm});
            skLineSegment(sketch, "E21.6.39", {"start": v(6.35, 228.6) * mm, "end": v(12.7, 228.6) * mm});
            skArc(sketch, "E21.6.40", {"start": v(0, 361.95) * mm, "mid": v(1.86, 366.44) * mm, "end": v(6.35, 368.3) * mm});
            skLineSegment(sketch, "E21.6.41", {"start": v(6.35, 127) * mm, "end": v(12.7, 127) * mm});
            skArc(sketch, "E21.6.42", {"start": v(0, 222.25) * mm, "mid": v(1.86, 226.74) * mm, "end": v(6.35, 228.6) * mm});
            skLineSegment(sketch, "E21.6.43", {"start": v(6.35, 406.4) * mm, "end": v(12.7, 406.4) * mm});
            skArc(sketch, "E21.6.44", {"start": v(0, 82.55) * mm, "mid": v(1.86, 87.04) * mm, "end": v(6.35, 88.9) * mm});
            skLineSegment(sketch, "E21.6.45", {"start": v(6.35, 88.9) * mm, "end": v(12.7, 88.9) * mm});
            skArc(sketch, "E21.6.46", {"start": v(0, 133.35) * mm, "mid": v(1.86, 128.86) * mm, "end": v(6.35, 127) * mm});
            skLineSegment(sketch, "E21.6.47", {"start": v(0, 412.75) * mm, "end": v(0, 406.4) * mm, "construction": true});
            skLineSegment(sketch, "E21.6.48", {"start": v(0, 133.35) * mm, "end": v(0, 127) * mm, "construction": true});
            skLineSegment(sketch, "E21.6.49", {"start": v(0, 273.05) * mm, "end": v(0, 266.7) * mm, "construction": true});
            skLineSegment(sketch, "E21.6.50", {"start": v(0, 266.7) * mm, "end": v(6.35, 266.7) * mm, "construction": true});
            skLineSegment(sketch, "E21.6.51", {"start": v(0, 127) * mm, "end": v(6.35, 127) * mm, "construction": true});
            skLineSegment(sketch, "E21.6.52", {"start": v(0, 406.4) * mm, "end": v(6.35, 406.4) * mm, "construction": true});
            skArc(sketch, "E21.6.53", {"start": v(0, 273.05) * mm, "mid": v(1.86, 268.56) * mm, "end": v(6.35, 266.7) * mm});
            skArc(sketch, "E21.6.54", {"start": v(0, 412.75) * mm, "mid": v(1.86, 408.26) * mm, "end": v(6.35, 406.4) * mm});
            skLineSegment(sketch, "E21.7.0", {"start": v(-224.5, 224.5) * mm, "end": v(-193.08, 193.08) * mm});
            skLineSegment(sketch, "E21.7.1", {"start": v(-89.8, 89.8) * mm, "end": v(-76.33, 76.33) * mm, "construction": true});
            skArc(sketch, "E21.7.2", {"start": v(-278.39, 296.35) * mm, "mid": v(-274.67, 305.33) * mm, "end": v(-278.39, 314.3) * mm});
            skLineSegment(sketch, "E21.7.3", {"start": v(-323.29, 323.29) * mm, "end": v(-224.5, 224.5) * mm, "construction": true});
            skLineSegment(sketch, "E21.7.4", {"start": v(-175.11, 175.11) * mm, "end": v(-139.2, 211.04) * mm, "construction": true});
            skPoint(sketch, "E21.7.5", {"position": v(-188.59, 188.59) * mm});
            skArc(sketch, "E21.7.6", {"start": v(-251.45, 269.4) * mm, "mid": v(-242.47, 273.13) * mm, "end": v(-233.49, 269.4) * mm});
            skLineSegment(sketch, "E21.7.7", {"start": v(-215.53, 287.37) * mm, "end": v(-237.98, 309.82) * mm});
            skLineSegment(sketch, "E21.7.8", {"start": v(-260.43, 332.27) * mm, "end": v(-237.98, 309.82) * mm});
            skPoint(sketch, "E21.7.9", {"position": v(-260.43, 314.3) * mm});
            skArc(sketch, "E21.7.10", {"start": v(-260.43, 332.27) * mm, "mid": v(-278.39, 332.27) * mm, "end": v(-278.39, 314.3) * mm});
            skLineSegment(sketch, "E21.7.11", {"start": v(-273.9, 273.9) * mm, "end": v(-237.98, 309.82) * mm, "construction": true});
            skLineSegment(sketch, "E21.7.12", {"start": v(-157.15, 157.15) * mm, "end": v(-125.72, 125.72) * mm});
            skArc(sketch, "E21.7.13", {"start": v(-179.6, 197.57) * mm, "mid": v(-175.89, 206.55) * mm, "end": v(-179.6, 215.53) * mm});
            skArc(sketch, "E21.7.14", {"start": v(-17.96, 89.8) * mm, "mid": v(-17.96, 71.84) * mm, "end": v(-35.92, 71.84) * mm});
            skArc(sketch, "E21.7.15", {"start": v(-161.64, 233.49) * mm, "mid": v(-179.6, 233.49) * mm, "end": v(-179.6, 215.53) * mm});
            skLineSegment(sketch, "E21.7.16", {"start": v(-188.59, 188.59) * mm, "end": v(-175.11, 175.11) * mm, "construction": true});
            skArc(sketch, "E21.7.17", {"start": v(-80.82, 98.78) * mm, "mid": v(-77.1, 107.76) * mm, "end": v(-80.82, 116.74) * mm});
            skLineSegment(sketch, "E21.7.18", {"start": v(-161.64, 233.49) * mm, "end": v(-139.2, 211.04) * mm});
            skLineSegment(sketch, "E21.7.19", {"start": v(-62.86, 134.7) * mm, "end": v(-40.41, 112.25) * mm});
            skLineSegment(sketch, "E21.7.20", {"start": v(-116.74, 188.59) * mm, "end": v(-139.2, 211.04) * mm});
            skLineSegment(sketch, "E21.7.21", {"start": v(-278.39, 314.3) * mm, "end": v(-233.49, 269.4) * mm, "construction": true});
            skLineSegment(sketch, "E21.7.22", {"start": v(-76.33, 76.33) * mm, "end": v(-40.41, 112.25) * mm, "construction": true});
            skPoint(sketch, "E21.7.23", {"position": v(-62.86, 116.74) * mm});
            skLineSegment(sketch, "E21.7.24", {"start": v(-125.72, 125.72) * mm, "end": v(-94.3, 94.3) * mm});
            skLineSegment(sketch, "E21.7.25", {"start": v(-58.37, 58.37) * mm, "end": v(0, 0) * mm});
            skLineSegment(sketch, "E21.7.26", {"start": v(-17.96, 89.8) * mm, "end": v(-40.41, 112.25) * mm});
            skArc(sketch, "E21.7.27", {"start": v(-116.74, 188.59) * mm, "mid": v(-116.74, 170.62) * mm, "end": v(-134.7, 170.62) * mm});
            skArc(sketch, "E21.7.28", {"start": v(-53.88, 71.84) * mm, "mid": v(-44.9, 75.56) * mm, "end": v(-35.92, 71.84) * mm});
            skPoint(sketch, "E21.7.29", {"position": v(-287.37, 287.37) * mm});
            skArc(sketch, "E21.7.30", {"start": v(-152.66, 170.62) * mm, "mid": v(-143.68, 174.34) * mm, "end": v(-134.7, 170.62) * mm});
            skArc(sketch, "E21.7.31", {"start": v(-62.86, 134.7) * mm, "mid": v(-80.82, 134.7) * mm, "end": v(-80.82, 116.74) * mm});
            skPoint(sketch, "E21.7.32", {"position": v(-161.64, 215.53) * mm});
            skArc(sketch, "E21.7.33", {"start": v(-215.53, 287.37) * mm, "mid": v(-215.53, 269.4) * mm, "end": v(-233.49, 269.4) * mm});
            skLineSegment(sketch, "E21.7.34", {"start": v(-255.94, 255.94) * mm, "end": v(-224.5, 224.5) * mm});
            skLineSegment(sketch, "E21.7.35", {"start": v(-323.29, 323.29) * mm, "end": v(-291.86, 291.86) * mm});
            skLineSegment(sketch, "E21.7.36", {"start": v(-287.37, 287.37) * mm, "end": v(-273.9, 273.9) * mm, "construction": true});
            skLineSegment(sketch, "E21.7.37", {"start": v(-184.1, 193.08) * mm, "end": v(-179.6, 197.57) * mm});
            skLineSegment(sketch, "E21.7.38", {"start": v(-255.94, 264.92) * mm, "end": v(-251.45, 269.4) * mm});
            skLineSegment(sketch, "E21.7.39", {"start": v(-157.15, 166.13) * mm, "end": v(-152.66, 170.62) * mm});
            skArc(sketch, "E21.7.40", {"start": v(-255.94, 255.94) * mm, "mid": v(-257.8, 260.43) * mm, "end": v(-255.94, 264.92) * mm});
            skLineSegment(sketch, "E21.7.41", {"start": v(-85.31, 94.3) * mm, "end": v(-80.82, 98.78) * mm});
            skArc(sketch, "E21.7.42", {"start": v(-157.15, 157.15) * mm, "mid": v(-159.01, 161.64) * mm, "end": v(-157.15, 166.13) * mm});
            skLineSegment(sketch, "E21.7.43", {"start": v(-282.88, 291.86) * mm, "end": v(-278.39, 296.35) * mm});
            skArc(sketch, "E21.7.44", {"start": v(-58.37, 58.37) * mm, "mid": v(-60.23, 62.86) * mm, "end": v(-58.37, 67.35) * mm});
            skLineSegment(sketch, "E21.7.45", {"start": v(-58.37, 67.35) * mm, "end": v(-53.88, 71.84) * mm});
            skArc(sketch, "E21.7.46", {"start": v(-94.3, 94.3) * mm, "mid": v(-89.8, 92.43) * mm, "end": v(-85.31, 94.3) * mm});
            skLineSegment(sketch, "E21.7.47", {"start": v(-291.86, 291.86) * mm, "end": v(-287.37, 287.37) * mm, "construction": true});
            skLineSegment(sketch, "E21.7.48", {"start": v(-94.3, 94.3) * mm, "end": v(-89.8, 89.8) * mm, "construction": true});
            skLineSegment(sketch, "E21.7.49", {"start": v(-193.08, 193.08) * mm, "end": v(-188.59, 188.59) * mm, "construction": true});
            skLineSegment(sketch, "E21.7.50", {"start": v(-188.59, 188.59) * mm, "end": v(-184.1, 193.08) * mm, "construction": true});
            skLineSegment(sketch, "E21.7.51", {"start": v(-89.8, 89.8) * mm, "end": v(-85.31, 94.3) * mm, "construction": true});
            skLineSegment(sketch, "E21.7.52", {"start": v(-287.37, 287.37) * mm, "end": v(-282.88, 291.86) * mm, "construction": true});
            skArc(sketch, "E21.7.53", {"start": v(-193.08, 193.08) * mm, "mid": v(-188.59, 191.22) * mm, "end": v(-184.1, 193.08) * mm});
            skArc(sketch, "E21.7.54", {"start": v(-291.86, 291.86) * mm, "mid": v(-287.37, 290) * mm, "end": v(-282.88, 291.86) * mm});
            skSolve(sketch);
        }
        {
            var Q0;
            {var subQ1=sQuery(id+"F0.wireOp",EDGE,"E0");Q0=makeQuery(id+"F0.imprint","IMPRINT",FACE,{"disambiguationData":[TD([[makeQuery(id+"F0.imprint","IMPRINT",EDGE,{"derivedFrom":subQ1}),-1.0]])]});}
            extrude(context, id + "F1", {"entities" : qUnion([Q0]), "depth" : 5 * mm});
        }
        {
            var Q0;
            {var subQ0=sQuery(id+"F0.wireOp",EDGE,"E0");Q0=makeQuery(id+"F0.imprint","IMPRINT",FACE,{"disambiguationData":[TD([[makeQuery(id+"F0.imprint","IMPRINT",EDGE,{"derivedFrom":subQ0}),1.0]])]});}
            extrude(context, id + "F2", {"entities" : qUnion([Q0]), "depth" : 5 * mm});
        }
        {
            var Q0;
            Q0=makeQuery(id+"F0.imprint","IMPRINT",FACE,{"disambiguationData":[TD([[makeQuery(id+"F0.imprint","IMPRINT",EDGE,{"derivedFrom":sQuery(id+"F0.wireOp",EDGE,"E21.6.0")}),-1.0]])]});
            extrude(context, id + "F3", {"entities" : qUnion([Q0]), "depth" : 5 * mm});
        }
        {
            var Q0;
            Q0=makeQuery(id+"F0.imprint","IMPRINT",FACE,{"disambiguationData":[TD([[makeQuery(id+"F0.imprint","IMPRINT",EDGE,{"derivedFrom":sQuery(id+"F0.wireOp",EDGE,"E21.5.0")}),-1.0]])]});
            extrude(context, id + "F4", {"entities" : qUnion([Q0]), "depth" : 5 * mm});
        }
        {
            var Q0;
            Q0=makeQuery(id+"F0.imprint","IMPRINT",FACE,{"disambiguationData":[TD([[makeQuery(id+"F0.imprint","IMPRINT",EDGE,{"derivedFrom":sQuery(id+"F0.wireOp",EDGE,"E21.4.0")}),-1.0]])]});
            extrude(context, id + "F5", {"entities" : qUnion([Q0]), "depth" : 5 * mm});
        }
        {
            var Q0;
            Q0=makeQuery(id+"F0.imprint","IMPRINT",FACE,{"disambiguationData":[TD([[makeQuery(id+"F0.imprint","IMPRINT",EDGE,{"derivedFrom":sQuery(id+"F0.wireOp",EDGE,"E21.3.0")}),-1.0]])]});
            extrude(context, id + "F6", {"entities" : qUnion([Q0]), "depth" : 5 * mm});
        }
        {
            var Q0;
            Q0=makeQuery(id+"F0.imprint","IMPRINT",FACE,{"disambiguationData":[TD([[makeQuery(id+"F0.imprint","IMPRINT",EDGE,{"derivedFrom":sQuery(id+"F0.wireOp",EDGE,"E21.2.0")}),-1.0]])]});
            extrude(context, id + "F7", {"entities" : qUnion([Q0]), "depth" : 5 * mm});
        }
        {
            var Q0;
            Q0=makeQuery(id+"F0.imprint","IMPRINT",FACE,{"disambiguationData":[TD([[makeQuery(id+"F0.imprint","IMPRINT",EDGE,{"derivedFrom":sQuery(id+"F0.wireOp",EDGE,"E21.1.0")}),-1.0]])]});
            extrude(context, id + "F8", {"entities" : qUnion([Q0]), "depth" : 5 * mm});
        }
    });
